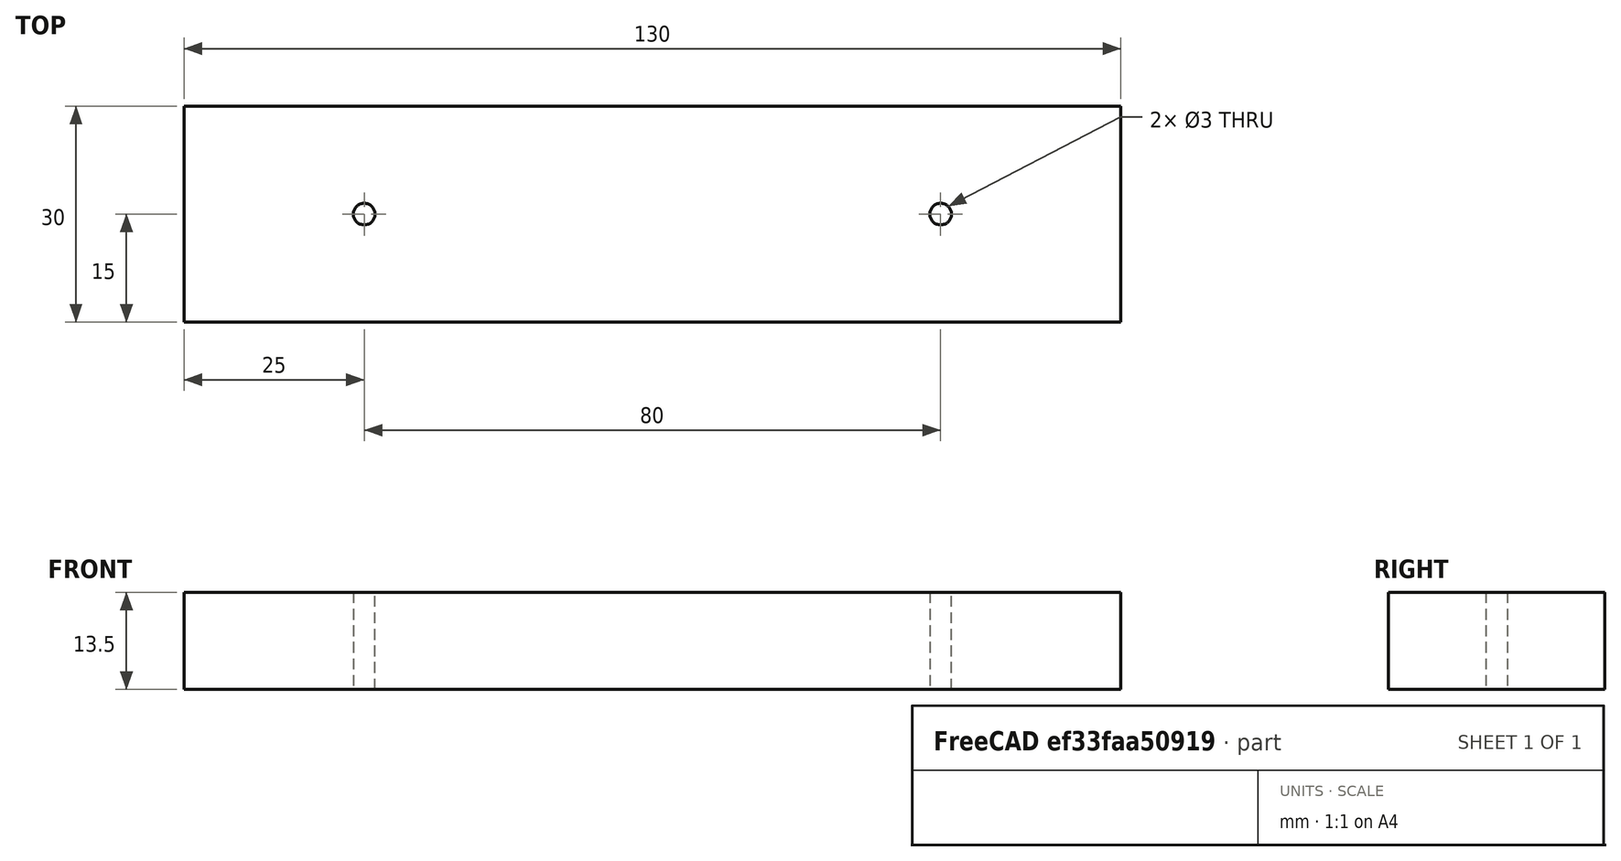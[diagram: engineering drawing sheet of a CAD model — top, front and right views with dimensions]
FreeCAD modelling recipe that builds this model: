
FCSTD DOCUMENT  (FreeCAD 0.19R24276 (Git))
Label: plate_130x30x13_5
License: All rights reserved
LicenseURL: http://en.wikipedia.org/wiki/All_rights_reserved
objects: Sketcher::SketchObject×1, PartDesign::Pad×1, PartDesign::Body×1
note: 4 computed .brp shape members not serialized (recipe doc carries the construction recipe); baked Part::Feature solids carry a one-line shape summary decoded from their .brp

FEATURE [Sketcher::SketchObject] Sketch
  FullyConstrained = true
  MapMode = 5
  Support = -> [XY_Plane]
  sketch-geometry (7):
    g0: LineSegment StartX=0 StartY=0 StartZ=0 EndX=130 EndY=0 EndZ=0
    g1: LineSegment StartX=130 StartY=0 StartZ=0 EndX=130 EndY=30 EndZ=0
    g2: LineSegment StartX=130 StartY=30 StartZ=0 EndX=0 EndY=30 EndZ=0
    g3: LineSegment StartX=0 StartY=30 StartZ=0 EndX=0 EndY=0 EndZ=0
    g4: Circle CenterX=25 CenterY=15 CenterZ=0 NormalX=0 NormalY=0 NormalZ=1 AngleXU=0 Radius=1.5
    g5: Circle CenterX=105 CenterY=15 CenterZ=0 NormalX=0 NormalY=0 NormalZ=1 AngleXU=0 Radius=1.5
    g6: LineSegment StartX=25 StartY=15 StartZ=0 EndX=105 EndY=15 EndZ=0
  constraints (19):
    c: Coincident(g0,g1)
    c: Coincident(g1,g2)
    c: Coincident(g2,g3)
    c: Coincident(g3,g0)
    c: Horizontal(g0)
    c: Horizontal(g2)
    c: Vertical(g1)
    c: Vertical(g3)
    c: Coincident(g0,g-1)
    c: DistanceX(g0,g0) = 130
    c: DistanceY(g3,g3) = 30
    c: Coincident(g6,g4)
    c: Coincident(g6,g5)
    c: Horizontal(g6)
    c: Diameter(g4) = 3
    c: Equal(g4,g5)
    c: DistanceX(g0,g4) = 25
    c: DistanceX(g5,g1) = 25
    c: DistanceY(g0,g4) = 15
FEATURE [PartDesign::Pad] Pad
  Direction = (1,1,1)
  Length = 13.5
  Length2 = 100
  Profile = -> Sketch
  Type = 0
FEATURE [PartDesign::Body] Body
  Group = -> [Sketch,Pad]
  Origin = -> Origin
  Tip = -> Pad
